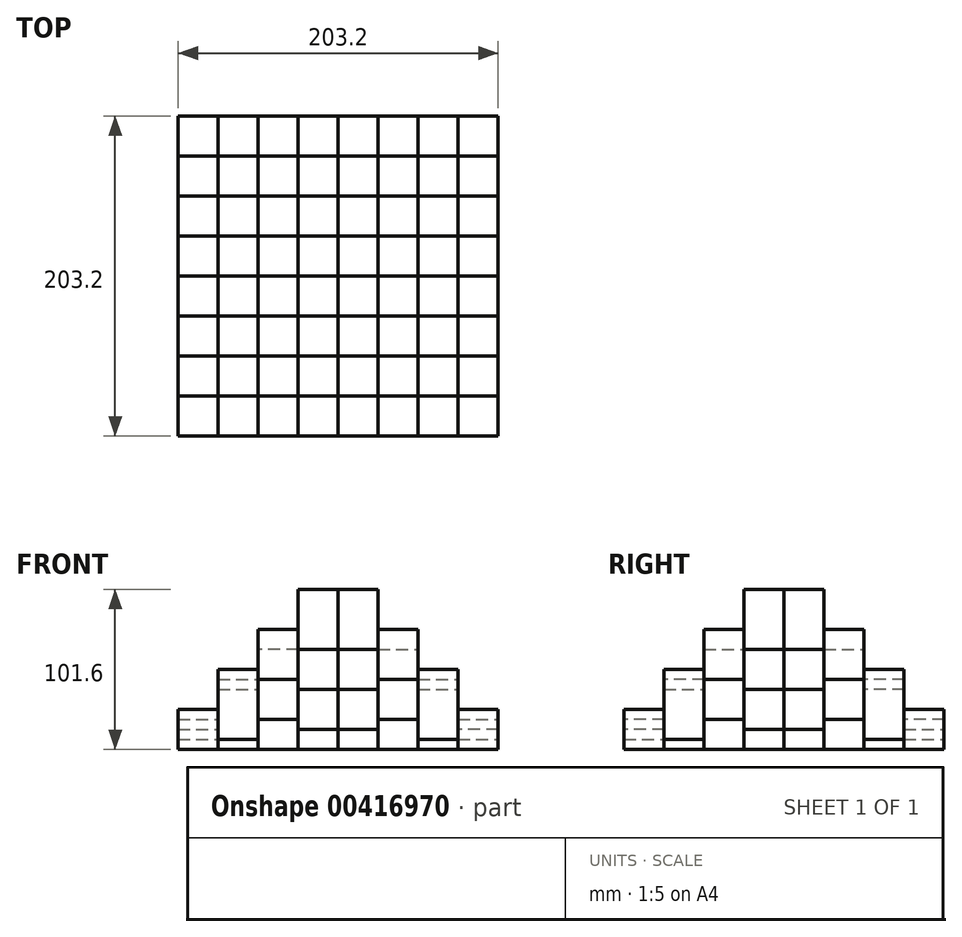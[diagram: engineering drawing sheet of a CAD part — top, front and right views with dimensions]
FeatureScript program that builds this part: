
annotation { "Feature Type Name" : "Feature", "Feature Type Description" : "" }
export const myFeature = defineFeature(function(context is Context, id is Id, definition is map)
    precondition{}
    {
        {
            var Q0;
            Q0=qCreatedBy(makeId("Top.planeOp"),FACE);
            var sketch = newSketch(context, id + "F0", { "sketchPlane" : qUnion([Q0])});
            skLineSegment(sketch, "E0.bottom", {"start": v(-101.6, 101.6) * mm, "end": v(101.6, 101.6) * mm});
            skLineSegment(sketch, "E0.top", {"start": v(-101.6, -101.6) * mm, "end": v(101.6, -101.6) * mm});
            skLineSegment(sketch, "E0.left", {"start": v(-101.6, 101.6) * mm, "end": v(-101.6, -101.6) * mm});
            skLineSegment(sketch, "E0.right", {"start": v(101.6, 101.6) * mm, "end": v(101.6, -101.6) * mm});
            skPoint(sketch, "E0.middle", {"position": v(0, 0) * mm});
            skLineSegment(sketch, "E1", {"start": v(0, 101.6) * mm, "end": v(0, -101.6) * mm});
            skLineSegment(sketch, "E2", {"start": v(-101.6, 0) * mm, "end": v(101.6, 0) * mm});
            skLineSegment(sketch, "E3", {"start": v(-101.6, 76.2) * mm, "end": v(101.6, 76.2) * mm});
            skLineSegment(sketch, "E4", {"start": v(-101.6, 50.8) * mm, "end": v(101.6, 50.8) * mm});
            skLineSegment(sketch, "E5", {"start": v(101.6, 25.4) * mm, "end": v(-101.6, 25.4) * mm});
            skLineSegment(sketch, "E6", {"start": v(-101.6, -25.4) * mm, "end": v(101.6, -25.4) * mm});
            skLineSegment(sketch, "E7", {"start": v(-101.6, -76.2) * mm, "end": v(101.6, -76.2) * mm});
            skLineSegment(sketch, "E8", {"start": v(-101.6, -50.8) * mm, "end": v(101.6, -50.8) * mm});
            skLineSegment(sketch, "E9", {"start": v(76.2, 101.6) * mm, "end": v(76.2, -101.6) * mm});
            skLineSegment(sketch, "E10", {"start": v(50.8, -101.6) * mm, "end": v(50.8, 101.6) * mm});
            skLineSegment(sketch, "E11", {"start": v(25.4, 101.6) * mm, "end": v(25.4, -101.6) * mm});
            skLineSegment(sketch, "E12", {"start": v(-25.4, -101.6) * mm, "end": v(-25.4, 101.6) * mm});
            skLineSegment(sketch, "E13", {"start": v(-50.8, 101.6) * mm, "end": v(-50.8, -101.6) * mm});
            skLineSegment(sketch, "E14", {"start": v(-76.2, -101.6) * mm, "end": v(-76.2, 101.6) * mm});
            skSolve(sketch);
        }
        {
            var Q0;
            {var subQ0=sQuery(id+"F0.wireOp",EDGE,"E0.left");var subQ1=sQuery(id+"F0.wireOp",EDGE,"E0.bottom");var subQ2=makeQuery(id+"F0.imprint","INTERSECT",VERTEX,{"derivedFrom":[subQ1,subQ0]});Q0=makeQuery(id+"F0.imprint","IMPRINT",FACE,{"disambiguationData":[TD([[makeQuery(id+"F0.imprint","IMPRINT",EDGE,{"disambiguationData":[TD([[subQ2,-1.0]])],"derivedFrom":subQ1}),-1.0]])]});}
            var Q1;
            {var subQ0=sQuery(id+"F0.wireOp",EDGE,"E0.right");var subQ1=sQuery(id+"F0.wireOp",EDGE,"E0.bottom");var subQ2=makeQuery(id+"F0.imprint","INTERSECT",VERTEX,{"derivedFrom":[subQ1,subQ0]});Q1=makeQuery(id+"F0.imprint","IMPRINT",FACE,{"disambiguationData":[TD([[makeQuery(id+"F0.imprint","IMPRINT",EDGE,{"disambiguationData":[TD([[subQ2,1.0]])],"derivedFrom":subQ1}),-1.0]])]});}
            var Q2;
            {var subQ0=sQuery(id+"F0.wireOp",EDGE,"E0.right");var subQ1=sQuery(id+"F0.wireOp",EDGE,"E0.top");var subQ2=makeQuery(id+"F0.imprint","INTERSECT",VERTEX,{"derivedFrom":[subQ1,subQ0]});Q2=makeQuery(id+"F0.imprint","IMPRINT",FACE,{"disambiguationData":[TD([[makeQuery(id+"F0.imprint","IMPRINT",EDGE,{"disambiguationData":[TD([[subQ2,1.0]])],"derivedFrom":subQ1}),1.0]])]});}
            var Q3;
            {var subQ0=sQuery(id+"F0.wireOp",EDGE,"E0.left");var subQ1=sQuery(id+"F0.wireOp",EDGE,"E0.top");var subQ2=makeQuery(id+"F0.imprint","INTERSECT",VERTEX,{"derivedFrom":[subQ1,subQ0]});Q3=makeQuery(id+"F0.imprint","IMPRINT",FACE,{"disambiguationData":[TD([[makeQuery(id+"F0.imprint","IMPRINT",EDGE,{"disambiguationData":[TD([[subQ2,-1.0]])],"derivedFrom":subQ1}),1.0]])]});}
            extrude(context, id + "F1", {"entities" : qUnion([Q0, Q1, Q2, Q3]), "depth" : 25.4 * mm, "offsetDistance" : 25.4 * mm});
        }
        {
            var Q0;
            {var subQ0=sQuery(id+"F0.wireOp",EDGE,"E14");var subQ1=sQuery(id+"F0.wireOp",EDGE,"E7");var subQ2=makeQuery(id+"F0.imprint","INTERSECT",VERTEX,{"derivedFrom":[subQ1,subQ0]});Q0=makeQuery(id+"F0.imprint","IMPRINT",FACE,{"disambiguationData":[TD([[makeQuery(id+"F0.imprint","IMPRINT",EDGE,{"disambiguationData":[TD([[subQ2,-1.0]])],"derivedFrom":subQ1}),1.0]])]});}
            var Q1;
            {var subQ0=sQuery(id+"F0.wireOp",EDGE,"E14");var subQ1=sQuery(id+"F0.wireOp",EDGE,"E3");var subQ2=makeQuery(id+"F0.imprint","INTERSECT",VERTEX,{"derivedFrom":[subQ1,subQ0]});Q1=makeQuery(id+"F0.imprint","IMPRINT",FACE,{"disambiguationData":[TD([[makeQuery(id+"F0.imprint","IMPRINT",EDGE,{"disambiguationData":[TD([[subQ2,-1.0]])],"derivedFrom":subQ1}),-1.0]])]});}
            var Q2;
            {var subQ0=sQuery(id+"F0.wireOp",EDGE,"E10");var subQ1=sQuery(id+"F0.wireOp",EDGE,"E3");var subQ2=makeQuery(id+"F0.imprint","INTERSECT",VERTEX,{"derivedFrom":[subQ1,subQ0]});Q2=makeQuery(id+"F0.imprint","IMPRINT",FACE,{"disambiguationData":[TD([[makeQuery(id+"F0.imprint","IMPRINT",EDGE,{"disambiguationData":[TD([[subQ2,-1.0]])],"derivedFrom":subQ1}),-1.0]])]});}
            var Q3;
            {var subQ0=sQuery(id+"F0.wireOp",EDGE,"E10");var subQ1=sQuery(id+"F0.wireOp",EDGE,"E7");var subQ2=makeQuery(id+"F0.imprint","INTERSECT",VERTEX,{"derivedFrom":[subQ1,subQ0]});Q3=makeQuery(id+"F0.imprint","IMPRINT",FACE,{"disambiguationData":[TD([[makeQuery(id+"F0.imprint","IMPRINT",EDGE,{"disambiguationData":[TD([[subQ2,-1.0]])],"derivedFrom":subQ1}),1.0]])]});}
            extrude(context, id + "F2", {"entities" : qUnion([Q0, Q1, Q2, Q3]), "depth" : 50.8 * mm, "offsetDistance" : 25.4 * mm});
        }
        {
            var Q0;
            {var subQ0=sQuery(id+"F0.wireOp",EDGE,"E13");var subQ1=sQuery(id+"F0.wireOp",EDGE,"E6");var subQ2=makeQuery(id+"F0.imprint","INTERSECT",VERTEX,{"derivedFrom":[subQ1,subQ0]});Q0=makeQuery(id+"F0.imprint","IMPRINT",FACE,{"disambiguationData":[TD([[makeQuery(id+"F0.imprint","IMPRINT",EDGE,{"disambiguationData":[TD([[subQ2,-1.0]])],"derivedFrom":subQ1}),-1.0]])]});}
            var Q1;
            {var subQ0=sQuery(id+"F0.wireOp",EDGE,"E13");var subQ1=sQuery(id+"F0.wireOp",EDGE,"E4");var subQ2=makeQuery(id+"F0.imprint","INTERSECT",VERTEX,{"derivedFrom":[subQ1,subQ0]});Q1=makeQuery(id+"F0.imprint","IMPRINT",FACE,{"disambiguationData":[TD([[makeQuery(id+"F0.imprint","IMPRINT",EDGE,{"disambiguationData":[TD([[subQ2,-1.0]])],"derivedFrom":subQ1}),-1.0]])]});}
            var Q2;
            {var subQ0=sQuery(id+"F0.wireOp",EDGE,"E11");var subQ1=sQuery(id+"F0.wireOp",EDGE,"E4");var subQ2=makeQuery(id+"F0.imprint","INTERSECT",VERTEX,{"derivedFrom":[subQ1,subQ0]});Q2=makeQuery(id+"F0.imprint","IMPRINT",FACE,{"disambiguationData":[TD([[makeQuery(id+"F0.imprint","IMPRINT",EDGE,{"disambiguationData":[TD([[subQ2,-1.0]])],"derivedFrom":subQ1}),-1.0]])]});}
            var Q3;
            {var subQ0=sQuery(id+"F0.wireOp",EDGE,"E11");var subQ1=sQuery(id+"F0.wireOp",EDGE,"E6");var subQ2=makeQuery(id+"F0.imprint","INTERSECT",VERTEX,{"derivedFrom":[subQ1,subQ0]});Q3=makeQuery(id+"F0.imprint","IMPRINT",FACE,{"disambiguationData":[TD([[makeQuery(id+"F0.imprint","IMPRINT",EDGE,{"disambiguationData":[TD([[subQ2,-1.0]])],"derivedFrom":subQ1}),-1.0]])]});}
            extrude(context, id + "F3", {"entities" : qUnion([Q0, Q1, Q2, Q3]), "depth" : 76.2 * mm, "offsetDistance" : 25.4 * mm});
        }
        {
            var Q0;
            {var subQ0=sQuery(id+"F0.wireOp",EDGE,"E5");var subQ1=sQuery(id+"F0.wireOp",EDGE,"E1");var subQ2=makeQuery(id+"F0.imprint","INTERSECT",VERTEX,{"derivedFrom":[subQ1,subQ0]});Q0=makeQuery(id+"F0.imprint","IMPRINT",FACE,{"disambiguationData":[TD([[makeQuery(id+"F0.imprint","IMPRINT",EDGE,{"disambiguationData":[TD([[subQ2,-1.0]])],"derivedFrom":subQ1}),-1.0]])]});}
            var Q1;
            {var subQ0=sQuery(id+"F0.wireOp",EDGE,"E2");var subQ1=sQuery(id+"F0.wireOp",EDGE,"E1");var subQ2=makeQuery(id+"F0.imprint","INTERSECT",VERTEX,{"derivedFrom":[subQ1,subQ0]});Q1=makeQuery(id+"F0.imprint","IMPRINT",FACE,{"disambiguationData":[TD([[makeQuery(id+"F0.imprint","IMPRINT",EDGE,{"disambiguationData":[TD([[subQ2,-1.0]])],"derivedFrom":subQ1}),1.0]])]});}
            extrude(context, id + "F4", {"entities" : qUnion([Q0, Q1]), "depth" : 101.6 * mm, "offsetDistance" : 25.4 * mm});
        }
        {
            var Q0;
            {var subQ0=sQuery(id+"F0.wireOp",EDGE,"E5");var subQ1=sQuery(id+"F0.wireOp",EDGE,"E1");var subQ2=makeQuery(id+"F0.imprint","INTERSECT",VERTEX,{"derivedFrom":[subQ1,subQ0]});Q0=makeQuery(id+"F0.imprint","IMPRINT",FACE,{"disambiguationData":[TD([[makeQuery(id+"F0.imprint","IMPRINT",EDGE,{"disambiguationData":[TD([[subQ2,-1.0]])],"derivedFrom":subQ1}),1.0]])]});}
            var Q1;
            {var subQ0=sQuery(id+"F0.wireOp",EDGE,"E2");var subQ1=sQuery(id+"F0.wireOp",EDGE,"E1");var subQ2=makeQuery(id+"F0.imprint","INTERSECT",VERTEX,{"derivedFrom":[subQ1,subQ0]});Q1=makeQuery(id+"F0.imprint","IMPRINT",FACE,{"disambiguationData":[TD([[makeQuery(id+"F0.imprint","IMPRINT",EDGE,{"disambiguationData":[TD([[subQ2,-1.0]])],"derivedFrom":subQ1}),-1.0]])]});}
            extrude(context, id + "F5", {"entities" : qUnion([Q0, Q1]), "depth" : 101.6 * mm, "offsetDistance" : 25.4 * mm});
        }
        {
            var Q0;
            {var subQ0=sQuery(id+"F0.wireOp",EDGE,"E2");var subQ1=sQuery(id+"F0.wireOp",EDGE,"E0.left");var subQ2=makeQuery(id+"F0.imprint","INTERSECT",VERTEX,{"derivedFrom":[subQ1,subQ0]});Q0=makeQuery(id+"F0.imprint","IMPRINT",FACE,{"disambiguationData":[TD([[makeQuery(id+"F0.imprint","IMPRINT",EDGE,{"disambiguationData":[TD([[subQ2,1.0]])],"derivedFrom":subQ1}),1.0]])]});}
            var Q1;
            {var subQ0=sQuery(id+"F0.wireOp",EDGE,"E1");var subQ1=sQuery(id+"F0.wireOp",EDGE,"E0.top");var subQ2=makeQuery(id+"F0.imprint","INTERSECT",VERTEX,{"derivedFrom":[subQ1,subQ0]});Q1=makeQuery(id+"F0.imprint","IMPRINT",FACE,{"disambiguationData":[TD([[makeQuery(id+"F0.imprint","IMPRINT",EDGE,{"disambiguationData":[TD([[subQ2,1.0]])],"derivedFrom":subQ1}),1.0]])]});}
            var Q2;
            {var subQ0=sQuery(id+"F0.wireOp",EDGE,"E2");var subQ1=sQuery(id+"F0.wireOp",EDGE,"E0.right");var subQ2=makeQuery(id+"F0.imprint","INTERSECT",VERTEX,{"derivedFrom":[subQ1,subQ0]});Q2=makeQuery(id+"F0.imprint","IMPRINT",FACE,{"disambiguationData":[TD([[makeQuery(id+"F0.imprint","IMPRINT",EDGE,{"disambiguationData":[TD([[subQ2,-1.0]])],"derivedFrom":subQ1}),-1.0]])]});}
            var Q3;
            {var subQ0=sQuery(id+"F0.wireOp",EDGE,"E1");var subQ1=sQuery(id+"F0.wireOp",EDGE,"E0.bottom");var subQ2=makeQuery(id+"F0.imprint","INTERSECT",VERTEX,{"derivedFrom":[subQ1,subQ0]});Q3=makeQuery(id+"F0.imprint","IMPRINT",FACE,{"disambiguationData":[TD([[makeQuery(id+"F0.imprint","IMPRINT",EDGE,{"disambiguationData":[TD([[subQ2,-1.0]])],"derivedFrom":subQ1}),-1.0]])]});}
            extrude(context, id + "F6", {"entities" : qUnion([Q0, Q1, Q2, Q3]), "depth" : 12.7 * mm, "offsetDistance" : 25.4 * mm});
        }
        {
            var Q0;
            {var subQ0=sQuery(id+"F0.wireOp",EDGE,"E1");var subQ1=sQuery(id+"F0.wireOp",EDGE,"E0.bottom");var subQ2=makeQuery(id+"F0.imprint","INTERSECT",VERTEX,{"derivedFrom":[subQ1,subQ0]});Q0=makeQuery(id+"F0.imprint","IMPRINT",FACE,{"disambiguationData":[TD([[makeQuery(id+"F0.imprint","IMPRINT",EDGE,{"disambiguationData":[TD([[subQ2,1.0]])],"derivedFrom":subQ1}),-1.0]])]});}
            var Q1;
            {var subQ0=sQuery(id+"F0.wireOp",EDGE,"E2");var subQ1=sQuery(id+"F0.wireOp",EDGE,"E0.right");var subQ2=makeQuery(id+"F0.imprint","INTERSECT",VERTEX,{"derivedFrom":[subQ1,subQ0]});Q1=makeQuery(id+"F0.imprint","IMPRINT",FACE,{"disambiguationData":[TD([[makeQuery(id+"F0.imprint","IMPRINT",EDGE,{"disambiguationData":[TD([[subQ2,1.0]])],"derivedFrom":subQ1}),-1.0]])]});}
            var Q2;
            {var subQ0=sQuery(id+"F0.wireOp",EDGE,"E1");var subQ1=sQuery(id+"F0.wireOp",EDGE,"E0.top");var subQ2=makeQuery(id+"F0.imprint","INTERSECT",VERTEX,{"derivedFrom":[subQ1,subQ0]});Q2=makeQuery(id+"F0.imprint","IMPRINT",FACE,{"disambiguationData":[TD([[makeQuery(id+"F0.imprint","IMPRINT",EDGE,{"disambiguationData":[TD([[subQ2,-1.0]])],"derivedFrom":subQ1}),1.0]])]});}
            var Q3;
            {var subQ0=sQuery(id+"F0.wireOp",EDGE,"E2");var subQ1=sQuery(id+"F0.wireOp",EDGE,"E0.left");var subQ2=makeQuery(id+"F0.imprint","INTERSECT",VERTEX,{"derivedFrom":[subQ1,subQ0]});Q3=makeQuery(id+"F0.imprint","IMPRINT",FACE,{"disambiguationData":[TD([[makeQuery(id+"F0.imprint","IMPRINT",EDGE,{"disambiguationData":[TD([[subQ2,-1.0]])],"derivedFrom":subQ1}),1.0]])]});}
            extrude(context, id + "F7", {"entities" : qUnion([Q0, Q1, Q2, Q3]), "depth" : 12.7 * mm, "offsetDistance" : 25.4 * mm});
        }
        {
            var Q0;
            {var subQ0=sQuery(id+"F0.wireOp",EDGE,"E14");var subQ1=sQuery(id+"F0.wireOp",EDGE,"E2");var subQ2=makeQuery(id+"F0.imprint","INTERSECT",VERTEX,{"derivedFrom":[subQ1,subQ0]});Q0=makeQuery(id+"F0.imprint","IMPRINT",FACE,{"disambiguationData":[TD([[makeQuery(id+"F0.imprint","IMPRINT",EDGE,{"disambiguationData":[TD([[subQ2,-1.0]])],"derivedFrom":subQ1}),-1.0]])]});}
            var Q1;
            {var subQ0=sQuery(id+"F0.wireOp",EDGE,"E8");var subQ1=sQuery(id+"F0.wireOp",EDGE,"E1");var subQ2=makeQuery(id+"F0.imprint","INTERSECT",VERTEX,{"derivedFrom":[subQ1,subQ0]});Q1=makeQuery(id+"F0.imprint","IMPRINT",FACE,{"disambiguationData":[TD([[makeQuery(id+"F0.imprint","IMPRINT",EDGE,{"disambiguationData":[TD([[subQ2,-1.0]])],"derivedFrom":subQ1}),-1.0]])]});}
            var Q2;
            {var subQ0=sQuery(id+"F0.wireOp",EDGE,"E10");var subQ1=sQuery(id+"F0.wireOp",EDGE,"E2");var subQ2=makeQuery(id+"F0.imprint","INTERSECT",VERTEX,{"derivedFrom":[subQ1,subQ0]});Q2=makeQuery(id+"F0.imprint","IMPRINT",FACE,{"disambiguationData":[TD([[makeQuery(id+"F0.imprint","IMPRINT",EDGE,{"disambiguationData":[TD([[subQ2,-1.0]])],"derivedFrom":subQ1}),-1.0]])]});}
            var Q3;
            {var subQ0=sQuery(id+"F0.wireOp",EDGE,"E3");var subQ1=sQuery(id+"F0.wireOp",EDGE,"E1");var subQ2=makeQuery(id+"F0.imprint","INTERSECT",VERTEX,{"derivedFrom":[subQ1,subQ0]});Q3=makeQuery(id+"F0.imprint","IMPRINT",FACE,{"disambiguationData":[TD([[makeQuery(id+"F0.imprint","IMPRINT",EDGE,{"disambiguationData":[TD([[subQ2,-1.0]])],"derivedFrom":subQ1}),1.0]])]});}
            extrude(context, id + "F8", {"entities" : qUnion([Q0, Q1, Q2, Q3]), "depth" : 38.1 * mm, "offsetDistance" : 25.4 * mm});
        }
        {
            var Q0;
            {var subQ0=sQuery(id+"F0.wireOp",EDGE,"E14");var subQ1=sQuery(id+"F0.wireOp",EDGE,"E2");var subQ2=makeQuery(id+"F0.imprint","INTERSECT",VERTEX,{"derivedFrom":[subQ1,subQ0]});Q0=makeQuery(id+"F0.imprint","IMPRINT",FACE,{"disambiguationData":[TD([[makeQuery(id+"F0.imprint","IMPRINT",EDGE,{"disambiguationData":[TD([[subQ2,-1.0]])],"derivedFrom":subQ1}),1.0]])]});}
            var Q1;
            {var subQ0=sQuery(id+"F0.wireOp",EDGE,"E8");var subQ1=sQuery(id+"F0.wireOp",EDGE,"E1");var subQ2=makeQuery(id+"F0.imprint","INTERSECT",VERTEX,{"derivedFrom":[subQ1,subQ0]});Q1=makeQuery(id+"F0.imprint","IMPRINT",FACE,{"disambiguationData":[TD([[makeQuery(id+"F0.imprint","IMPRINT",EDGE,{"disambiguationData":[TD([[subQ2,-1.0]])],"derivedFrom":subQ1}),1.0]])]});}
            var Q2;
            {var subQ0=sQuery(id+"F0.wireOp",EDGE,"E10");var subQ1=sQuery(id+"F0.wireOp",EDGE,"E2");var subQ2=makeQuery(id+"F0.imprint","INTERSECT",VERTEX,{"derivedFrom":[subQ1,subQ0]});Q2=makeQuery(id+"F0.imprint","IMPRINT",FACE,{"disambiguationData":[TD([[makeQuery(id+"F0.imprint","IMPRINT",EDGE,{"disambiguationData":[TD([[subQ2,-1.0]])],"derivedFrom":subQ1}),1.0]])]});}
            var Q3;
            {var subQ0=sQuery(id+"F0.wireOp",EDGE,"E3");var subQ1=sQuery(id+"F0.wireOp",EDGE,"E1");var subQ2=makeQuery(id+"F0.imprint","INTERSECT",VERTEX,{"derivedFrom":[subQ1,subQ0]});Q3=makeQuery(id+"F0.imprint","IMPRINT",FACE,{"disambiguationData":[TD([[makeQuery(id+"F0.imprint","IMPRINT",EDGE,{"disambiguationData":[TD([[subQ2,-1.0]])],"derivedFrom":subQ1}),-1.0]])]});}
            extrude(context, id + "F9", {"entities" : qUnion([Q0, Q1, Q2, Q3]), "depth" : 38.1 * mm, "offsetDistance" : 25.4 * mm});
        }
        {
            var Q0;
            {var subQ0=sQuery(id+"F0.wireOp",EDGE,"E13");var subQ1=sQuery(id+"F0.wireOp",EDGE,"E2");var subQ2=makeQuery(id+"F0.imprint","INTERSECT",VERTEX,{"derivedFrom":[subQ1,subQ0]});Q0=makeQuery(id+"F0.imprint","IMPRINT",FACE,{"disambiguationData":[TD([[makeQuery(id+"F0.imprint","IMPRINT",EDGE,{"disambiguationData":[TD([[subQ2,-1.0]])],"derivedFrom":subQ1}),-1.0]])]});}
            var Q1;
            {var subQ0=sQuery(id+"F0.wireOp",EDGE,"E6");var subQ1=sQuery(id+"F0.wireOp",EDGE,"E1");var subQ2=makeQuery(id+"F0.imprint","INTERSECT",VERTEX,{"derivedFrom":[subQ1,subQ0]});Q1=makeQuery(id+"F0.imprint","IMPRINT",FACE,{"disambiguationData":[TD([[makeQuery(id+"F0.imprint","IMPRINT",EDGE,{"disambiguationData":[TD([[subQ2,-1.0]])],"derivedFrom":subQ1}),1.0]])]});}
            var Q2;
            {var subQ0=sQuery(id+"F0.wireOp",EDGE,"E11");var subQ1=sQuery(id+"F0.wireOp",EDGE,"E2");var subQ2=makeQuery(id+"F0.imprint","INTERSECT",VERTEX,{"derivedFrom":[subQ1,subQ0]});Q2=makeQuery(id+"F0.imprint","IMPRINT",FACE,{"disambiguationData":[TD([[makeQuery(id+"F0.imprint","IMPRINT",EDGE,{"disambiguationData":[TD([[subQ2,-1.0]])],"derivedFrom":subQ1}),1.0]])]});}
            var Q3;
            {var subQ0=sQuery(id+"F0.wireOp",EDGE,"E4");var subQ1=sQuery(id+"F0.wireOp",EDGE,"E1");var subQ2=makeQuery(id+"F0.imprint","INTERSECT",VERTEX,{"derivedFrom":[subQ1,subQ0]});Q3=makeQuery(id+"F0.imprint","IMPRINT",FACE,{"disambiguationData":[TD([[makeQuery(id+"F0.imprint","IMPRINT",EDGE,{"disambiguationData":[TD([[subQ2,-1.0]])],"derivedFrom":subQ1}),-1.0]])]});}
            extrude(context, id + "F10", {"entities" : qUnion([Q0, Q1, Q2, Q3]), "depth" : 63.5 * mm, "offsetDistance" : 25.4 * mm});
        }
        {
            var Q0;
            {var subQ0=sQuery(id+"F0.wireOp",EDGE,"E13");var subQ1=sQuery(id+"F0.wireOp",EDGE,"E2");var subQ2=makeQuery(id+"F0.imprint","INTERSECT",VERTEX,{"derivedFrom":[subQ1,subQ0]});Q0=makeQuery(id+"F0.imprint","IMPRINT",FACE,{"disambiguationData":[TD([[makeQuery(id+"F0.imprint","IMPRINT",EDGE,{"disambiguationData":[TD([[subQ2,-1.0]])],"derivedFrom":subQ1}),1.0]])]});}
            var Q1;
            {var subQ0=sQuery(id+"F0.wireOp",EDGE,"E6");var subQ1=sQuery(id+"F0.wireOp",EDGE,"E1");var subQ2=makeQuery(id+"F0.imprint","INTERSECT",VERTEX,{"derivedFrom":[subQ1,subQ0]});Q1=makeQuery(id+"F0.imprint","IMPRINT",FACE,{"disambiguationData":[TD([[makeQuery(id+"F0.imprint","IMPRINT",EDGE,{"disambiguationData":[TD([[subQ2,-1.0]])],"derivedFrom":subQ1}),-1.0]])]});}
            var Q2;
            {var subQ0=sQuery(id+"F0.wireOp",EDGE,"E11");var subQ1=sQuery(id+"F0.wireOp",EDGE,"E2");var subQ2=makeQuery(id+"F0.imprint","INTERSECT",VERTEX,{"derivedFrom":[subQ1,subQ0]});Q2=makeQuery(id+"F0.imprint","IMPRINT",FACE,{"disambiguationData":[TD([[makeQuery(id+"F0.imprint","IMPRINT",EDGE,{"disambiguationData":[TD([[subQ2,-1.0]])],"derivedFrom":subQ1}),-1.0]])]});}
            var Q3;
            {var subQ0=sQuery(id+"F0.wireOp",EDGE,"E4");var subQ1=sQuery(id+"F0.wireOp",EDGE,"E1");var subQ2=makeQuery(id+"F0.imprint","INTERSECT",VERTEX,{"derivedFrom":[subQ1,subQ0]});Q3=makeQuery(id+"F0.imprint","IMPRINT",FACE,{"disambiguationData":[TD([[makeQuery(id+"F0.imprint","IMPRINT",EDGE,{"disambiguationData":[TD([[subQ2,-1.0]])],"derivedFrom":subQ1}),1.0]])]});}
            extrude(context, id + "F11", {"entities" : qUnion([Q0, Q1, Q2, Q3]), "depth" : 63.5 * mm, "offsetDistance" : 25.4 * mm});
        }
        {
            var Q0;
            {var subQ0=sQuery(id+"F0.wireOp",EDGE,"E12");var subQ1=sQuery(id+"F0.wireOp",EDGE,"E0.top");var subQ2=makeQuery(id+"F0.imprint","INTERSECT",VERTEX,{"derivedFrom":[subQ1,subQ0]});Q0=makeQuery(id+"F0.imprint","IMPRINT",FACE,{"disambiguationData":[TD([[makeQuery(id+"F0.imprint","IMPRINT",EDGE,{"disambiguationData":[TD([[subQ2,1.0]])],"derivedFrom":subQ1}),1.0]])]});}
            var Q1;
            {var subQ0=sQuery(id+"F0.wireOp",EDGE,"E10");var subQ1=sQuery(id+"F0.wireOp",EDGE,"E0.top");var subQ2=makeQuery(id+"F0.imprint","INTERSECT",VERTEX,{"derivedFrom":[subQ1,subQ0]});Q1=makeQuery(id+"F0.imprint","IMPRINT",FACE,{"disambiguationData":[TD([[makeQuery(id+"F0.imprint","IMPRINT",EDGE,{"disambiguationData":[TD([[subQ2,1.0]])],"derivedFrom":subQ1}),1.0]])]});}
            var Q2;
            {var subQ0=sQuery(id+"F0.wireOp",EDGE,"E6");var subQ1=sQuery(id+"F0.wireOp",EDGE,"E0.right");var subQ2=makeQuery(id+"F0.imprint","INTERSECT",VERTEX,{"derivedFrom":[subQ1,subQ0]});Q2=makeQuery(id+"F0.imprint","IMPRINT",FACE,{"disambiguationData":[TD([[makeQuery(id+"F0.imprint","IMPRINT",EDGE,{"disambiguationData":[TD([[subQ2,-1.0]])],"derivedFrom":subQ1}),-1.0]])]});}
            var Q3;
            {var subQ0=sQuery(id+"F0.wireOp",EDGE,"E4");var subQ1=sQuery(id+"F0.wireOp",EDGE,"E0.right");var subQ2=makeQuery(id+"F0.imprint","INTERSECT",VERTEX,{"derivedFrom":[subQ1,subQ0]});Q3=makeQuery(id+"F0.imprint","IMPRINT",FACE,{"disambiguationData":[TD([[makeQuery(id+"F0.imprint","IMPRINT",EDGE,{"disambiguationData":[TD([[subQ2,-1.0]])],"derivedFrom":subQ1}),-1.0]])]});}
            var Q4;
            {var subQ0=sQuery(id+"F0.wireOp",EDGE,"E10");var subQ1=sQuery(id+"F0.wireOp",EDGE,"E0.bottom");var subQ2=makeQuery(id+"F0.imprint","INTERSECT",VERTEX,{"derivedFrom":[subQ1,subQ0]});Q4=makeQuery(id+"F0.imprint","IMPRINT",FACE,{"disambiguationData":[TD([[makeQuery(id+"F0.imprint","IMPRINT",EDGE,{"disambiguationData":[TD([[subQ2,1.0]])],"derivedFrom":subQ1}),-1.0]])]});}
            var Q5;
            {var subQ0=sQuery(id+"F0.wireOp",EDGE,"E12");var subQ1=sQuery(id+"F0.wireOp",EDGE,"E0.bottom");var subQ2=makeQuery(id+"F0.imprint","INTERSECT",VERTEX,{"derivedFrom":[subQ1,subQ0]});Q5=makeQuery(id+"F0.imprint","IMPRINT",FACE,{"disambiguationData":[TD([[makeQuery(id+"F0.imprint","IMPRINT",EDGE,{"disambiguationData":[TD([[subQ2,1.0]])],"derivedFrom":subQ1}),-1.0]])]});}
            var Q6;
            {var subQ0=sQuery(id+"F0.wireOp",EDGE,"E4");var subQ1=sQuery(id+"F0.wireOp",EDGE,"E0.left");var subQ2=makeQuery(id+"F0.imprint","INTERSECT",VERTEX,{"derivedFrom":[subQ1,subQ0]});Q6=makeQuery(id+"F0.imprint","IMPRINT",FACE,{"disambiguationData":[TD([[makeQuery(id+"F0.imprint","IMPRINT",EDGE,{"disambiguationData":[TD([[subQ2,-1.0]])],"derivedFrom":subQ1}),1.0]])]});}
            var Q7;
            {var subQ0=sQuery(id+"F0.wireOp",EDGE,"E6");var subQ1=sQuery(id+"F0.wireOp",EDGE,"E0.left");var subQ2=makeQuery(id+"F0.imprint","INTERSECT",VERTEX,{"derivedFrom":[subQ1,subQ0]});Q7=makeQuery(id+"F0.imprint","IMPRINT",FACE,{"disambiguationData":[TD([[makeQuery(id+"F0.imprint","IMPRINT",EDGE,{"disambiguationData":[TD([[subQ2,-1.0]])],"derivedFrom":subQ1}),1.0]])]});}
            extrude(context, id + "F12", {"entities" : qUnion([Q0, Q1, Q2, Q3, Q4, Q5, Q6, Q7]), "depth" : 19.05 * mm, "offsetDistance" : 25.4 * mm});
        }
        {
            var Q0;
            {var subQ0=sQuery(id+"F0.wireOp",EDGE,"E14");var subQ1=sQuery(id+"F0.wireOp",EDGE,"E4");var subQ2=makeQuery(id+"F0.imprint","INTERSECT",VERTEX,{"derivedFrom":[subQ1,subQ0]});Q0=makeQuery(id+"F0.imprint","IMPRINT",FACE,{"disambiguationData":[TD([[makeQuery(id+"F0.imprint","IMPRINT",EDGE,{"disambiguationData":[TD([[subQ2,-1.0]])],"derivedFrom":subQ1}),-1.0]])]});}
            var Q1;
            {var subQ0=sQuery(id+"F0.wireOp",EDGE,"E14");var subQ1=sQuery(id+"F0.wireOp",EDGE,"E6");var subQ2=makeQuery(id+"F0.imprint","INTERSECT",VERTEX,{"derivedFrom":[subQ1,subQ0]});Q1=makeQuery(id+"F0.imprint","IMPRINT",FACE,{"disambiguationData":[TD([[makeQuery(id+"F0.imprint","IMPRINT",EDGE,{"disambiguationData":[TD([[subQ2,-1.0]])],"derivedFrom":subQ1}),-1.0]])]});}
            var Q2;
            {var subQ0=sQuery(id+"F0.wireOp",EDGE,"E13");var subQ1=sQuery(id+"F0.wireOp",EDGE,"E7");var subQ2=makeQuery(id+"F0.imprint","INTERSECT",VERTEX,{"derivedFrom":[subQ1,subQ0]});Q2=makeQuery(id+"F0.imprint","IMPRINT",FACE,{"disambiguationData":[TD([[makeQuery(id+"F0.imprint","IMPRINT",EDGE,{"disambiguationData":[TD([[subQ2,-1.0]])],"derivedFrom":subQ1}),1.0]])]});}
            var Q3;
            {var subQ0=sQuery(id+"F0.wireOp",EDGE,"E11");var subQ1=sQuery(id+"F0.wireOp",EDGE,"E7");var subQ2=makeQuery(id+"F0.imprint","INTERSECT",VERTEX,{"derivedFrom":[subQ1,subQ0]});Q3=makeQuery(id+"F0.imprint","IMPRINT",FACE,{"disambiguationData":[TD([[makeQuery(id+"F0.imprint","IMPRINT",EDGE,{"disambiguationData":[TD([[subQ2,-1.0]])],"derivedFrom":subQ1}),1.0]])]});}
            var Q4;
            {var subQ0=sQuery(id+"F0.wireOp",EDGE,"E10");var subQ1=sQuery(id+"F0.wireOp",EDGE,"E6");var subQ2=makeQuery(id+"F0.imprint","INTERSECT",VERTEX,{"derivedFrom":[subQ1,subQ0]});Q4=makeQuery(id+"F0.imprint","IMPRINT",FACE,{"disambiguationData":[TD([[makeQuery(id+"F0.imprint","IMPRINT",EDGE,{"disambiguationData":[TD([[subQ2,-1.0]])],"derivedFrom":subQ1}),-1.0]])]});}
            var Q5;
            {var subQ0=sQuery(id+"F0.wireOp",EDGE,"E10");var subQ1=sQuery(id+"F0.wireOp",EDGE,"E4");var subQ2=makeQuery(id+"F0.imprint","INTERSECT",VERTEX,{"derivedFrom":[subQ1,subQ0]});Q5=makeQuery(id+"F0.imprint","IMPRINT",FACE,{"disambiguationData":[TD([[makeQuery(id+"F0.imprint","IMPRINT",EDGE,{"disambiguationData":[TD([[subQ2,-1.0]])],"derivedFrom":subQ1}),-1.0]])]});}
            var Q6;
            {var subQ0=sQuery(id+"F0.wireOp",EDGE,"E11");var subQ1=sQuery(id+"F0.wireOp",EDGE,"E3");var subQ2=makeQuery(id+"F0.imprint","INTERSECT",VERTEX,{"derivedFrom":[subQ1,subQ0]});Q6=makeQuery(id+"F0.imprint","IMPRINT",FACE,{"disambiguationData":[TD([[makeQuery(id+"F0.imprint","IMPRINT",EDGE,{"disambiguationData":[TD([[subQ2,-1.0]])],"derivedFrom":subQ1}),-1.0]])]});}
            var Q7;
            {var subQ0=sQuery(id+"F0.wireOp",EDGE,"E13");var subQ1=sQuery(id+"F0.wireOp",EDGE,"E3");var subQ2=makeQuery(id+"F0.imprint","INTERSECT",VERTEX,{"derivedFrom":[subQ1,subQ0]});Q7=makeQuery(id+"F0.imprint","IMPRINT",FACE,{"disambiguationData":[TD([[makeQuery(id+"F0.imprint","IMPRINT",EDGE,{"disambiguationData":[TD([[subQ2,-1.0]])],"derivedFrom":subQ1}),-1.0]])]});}
            extrude(context, id + "F13", {"entities" : qUnion([Q0, Q1, Q2, Q3, Q4, Q5, Q6, Q7]), "depth" : 44.45 * mm, "offsetDistance" : 25.4 * mm});
        }
        {
            var Q0;
            {var subQ0=sQuery(id+"F0.wireOp",EDGE,"E3");var subQ1=sQuery(id+"F0.wireOp",EDGE,"E0.left");var subQ2=makeQuery(id+"F0.imprint","INTERSECT",VERTEX,{"derivedFrom":[subQ1,subQ0]});Q0=makeQuery(id+"F0.imprint","IMPRINT",FACE,{"disambiguationData":[TD([[makeQuery(id+"F0.imprint","IMPRINT",EDGE,{"disambiguationData":[TD([[subQ2,-1.0]])],"derivedFrom":subQ1}),1.0]])]});}
            var Q1;
            {var subQ0=sQuery(id+"F0.wireOp",EDGE,"E7");var subQ1=sQuery(id+"F0.wireOp",EDGE,"E0.left");var subQ2=makeQuery(id+"F0.imprint","INTERSECT",VERTEX,{"derivedFrom":[subQ1,subQ0]});Q1=makeQuery(id+"F0.imprint","IMPRINT",FACE,{"disambiguationData":[TD([[makeQuery(id+"F0.imprint","IMPRINT",EDGE,{"disambiguationData":[TD([[subQ2,1.0]])],"derivedFrom":subQ1}),1.0]])]});}
            var Q2;
            {var subQ0=sQuery(id+"F0.wireOp",EDGE,"E13");var subQ1=sQuery(id+"F0.wireOp",EDGE,"E0.bottom");var subQ2=makeQuery(id+"F0.imprint","INTERSECT",VERTEX,{"derivedFrom":[subQ1,subQ0]});Q2=makeQuery(id+"F0.imprint","IMPRINT",FACE,{"disambiguationData":[TD([[makeQuery(id+"F0.imprint","IMPRINT",EDGE,{"disambiguationData":[TD([[subQ2,1.0]])],"derivedFrom":subQ1}),-1.0]])]});}
            var Q3;
            {var subQ0=sQuery(id+"F0.wireOp",EDGE,"E9");var subQ1=sQuery(id+"F0.wireOp",EDGE,"E0.bottom");var subQ2=makeQuery(id+"F0.imprint","INTERSECT",VERTEX,{"derivedFrom":[subQ1,subQ0]});Q3=makeQuery(id+"F0.imprint","IMPRINT",FACE,{"disambiguationData":[TD([[makeQuery(id+"F0.imprint","IMPRINT",EDGE,{"disambiguationData":[TD([[subQ2,1.0]])],"derivedFrom":subQ1}),-1.0]])]});}
            var Q4;
            {var subQ0=sQuery(id+"F0.wireOp",EDGE,"E3");var subQ1=sQuery(id+"F0.wireOp",EDGE,"E0.right");var subQ2=makeQuery(id+"F0.imprint","INTERSECT",VERTEX,{"derivedFrom":[subQ1,subQ0]});Q4=makeQuery(id+"F0.imprint","IMPRINT",FACE,{"disambiguationData":[TD([[makeQuery(id+"F0.imprint","IMPRINT",EDGE,{"disambiguationData":[TD([[subQ2,-1.0]])],"derivedFrom":subQ1}),-1.0]])]});}
            var Q5;
            {var subQ0=sQuery(id+"F0.wireOp",EDGE,"E7");var subQ1=sQuery(id+"F0.wireOp",EDGE,"E0.right");var subQ2=makeQuery(id+"F0.imprint","INTERSECT",VERTEX,{"derivedFrom":[subQ1,subQ0]});Q5=makeQuery(id+"F0.imprint","IMPRINT",FACE,{"disambiguationData":[TD([[makeQuery(id+"F0.imprint","IMPRINT",EDGE,{"disambiguationData":[TD([[subQ2,1.0]])],"derivedFrom":subQ1}),-1.0]])]});}
            var Q6;
            {var subQ0=sQuery(id+"F0.wireOp",EDGE,"E9");var subQ1=sQuery(id+"F0.wireOp",EDGE,"E0.top");var subQ2=makeQuery(id+"F0.imprint","INTERSECT",VERTEX,{"derivedFrom":[subQ1,subQ0]});Q6=makeQuery(id+"F0.imprint","IMPRINT",FACE,{"disambiguationData":[TD([[makeQuery(id+"F0.imprint","IMPRINT",EDGE,{"disambiguationData":[TD([[subQ2,1.0]])],"derivedFrom":subQ1}),1.0]])]});}
            var Q7;
            {var subQ0=sQuery(id+"F0.wireOp",EDGE,"E13");var subQ1=sQuery(id+"F0.wireOp",EDGE,"E0.top");var subQ2=makeQuery(id+"F0.imprint","INTERSECT",VERTEX,{"derivedFrom":[subQ1,subQ0]});Q7=makeQuery(id+"F0.imprint","IMPRINT",FACE,{"disambiguationData":[TD([[makeQuery(id+"F0.imprint","IMPRINT",EDGE,{"disambiguationData":[TD([[subQ2,1.0]])],"derivedFrom":subQ1}),1.0]])]});}
            extrude(context, id + "F14", {"entities" : qUnion([Q0, Q1, Q2, Q3, Q4, Q5, Q6, Q7]), "depth" : 6.35 * mm, "offsetDistance" : 25.4 * mm});
        }
    });
